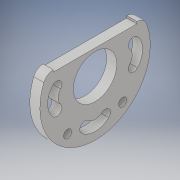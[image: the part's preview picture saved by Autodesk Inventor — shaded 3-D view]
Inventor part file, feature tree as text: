
AUTODESK INVENTOR PART (.ipt)
format: ipt  version: 2019 (Build 230136000, 136)  size: 154,112 bytes
history: native  units: mm
features: extrude x3, sketch x3
ambient origin geometry x8: Origin, YZ Plane, XZ Plane, XY Plane, X Axis, Y Axis, Z Axis, Center Point
bodies: Solid1 (feature_tree)
feature tree (6):
  extrude  "Extrusion1"  Depth=10.0mm
  extrude  "Extrusion2"  Depth=10.0mm TaperAngle=0.0deg
  extrude  "Extrusion3"  Depth=10.0mm
  sketch  "Sketch1"  dims[d4=10.0mm d5=10.0mm]
  sketch  "Sketch2"  dims[d6=10.0mm d7=0.0mm d9=10.0mm d10=0.0mm]
  sketch  "Sketch3"  dims[d11=8.0mm d12=8.0mm d13=10.0mm d14=0.0mm]
